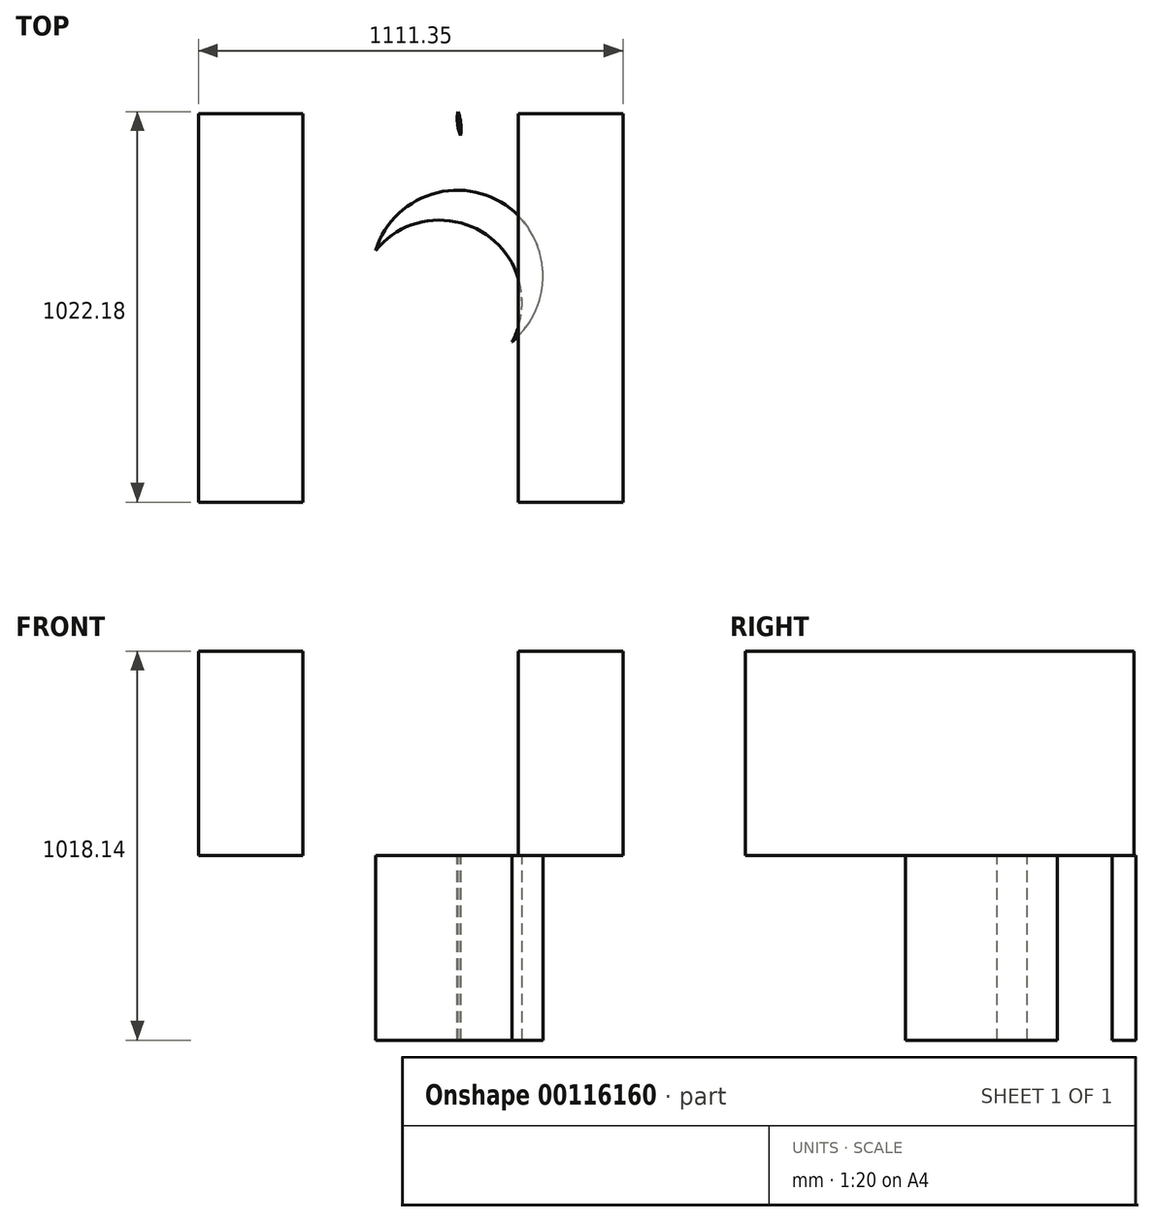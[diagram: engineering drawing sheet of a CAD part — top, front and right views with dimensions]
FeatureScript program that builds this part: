
annotation { "Feature Type Name" : "Feature", "Feature Type Description" : "" }
export const myFeature = defineFeature(function(context is Context, id is Id, definition is map)
    precondition{}
    {
        {
            var Q0;
            Q0=qCreatedBy(makeId("Front.planeOp"),FACE);
            var sketch = newSketch(context, id + "F0", { "sketchPlane" : qUnion([Q0])});
            skLineSegment(sketch, "E0.bottom", {"start": v(0, 0) * mm, "end": v(837.47, 0) * mm});
            skLineSegment(sketch, "E0.top", {"start": v(0, 535.38) * mm, "end": v(837.47, 535.38) * mm});
            skLineSegment(sketch, "E0.left", {"start": v(0, 0) * mm, "end": v(0, 535.38) * mm});
            skLineSegment(sketch, "E0.right", {"start": v(837.47, 0) * mm, "end": v(837.47, 535.38) * mm});
            skSolve(sketch);
        }
        {
            var Q0;
            Q0 = qSketchRegion(id + "F0", true);
            var Q1;
            Q1=sQuery(id+"F0.wireOp",EDGE,"E0.left");
            var Q2;
            Q2=sQuery(id+"F0.wireOp",EDGE,"E0.right");
            extrude(context, id + "F1", {"entities" : qUnion([Q0]), "bodyType" : ToolBodyType.SURFACE, "surfaceEntities" : qUnion([Q1, Q2]), "depth" : 1017.07 * mm});
        }
        {
            var Q0;
            Q0=qCreatedBy(makeId("Top.planeOp"),FACE);
            var sketch = newSketch(context, id + "F2", { "sketchPlane" : qUnion([Q0])});
            skArc(sketch, "E1", {"start": v(842.79, 0) * mm, "mid": v(81.24, 5.11) * mm, "end": v(547.08, -597.36) * mm});
            skArc(sketch, "E2", {"start": v(547.08, -597.36) * mm, "mid": v(489.15, -217.28) * mm, "end": v(180.8, -446.93) * mm});
            skArc(sketch, "E3", {"start": v(547.08, -597.36) * mm, "mid": v(477.47, -315.2) * mm, "end": v(189.96, -357.63) * mm});
            skArc(sketch, "E4", {"start": v(189.96, -75.06) * mm, "mid": v(81.98, -216.34) * mm, "end": v(189.96, -357.63) * mm});
            skArc(sketch, "E5", {"start": v(189.96, -75.06) * mm, "mid": v(403.04, -85.58) * mm, "end": v(256.29, 69.25) * mm});
            skArc(sketch, "E6", {"start": v(405.3, 5.11) * mm, "mid": v(558.05, -126.53) * mm, "end": v(606.3, 69.25) * mm});
            skSolve(sketch);
        }
        {
            var Q0;
            {var subQ0=sQuery(id+"F2.wireOp",EDGE,"E6");var subQ1=sQuery(id+"F2.wireOp",EDGE,"E5");var subQ2=makeQuery(id+"F2.imprint","INTERSECT",VERTEX,{"disambiguationData":[OD(0.0)],"derivedFrom":[subQ1,subQ0]});Q0=makeQuery(id+"F2.imprint","IMPRINT",FACE,{"disambiguationData":[TD([[makeQuery(id+"F2.imprint","IMPRINT",EDGE,{"disambiguationData":[TD([[subQ2,1.0]])],"derivedFrom":subQ1}),1.0]])]});}
            var Q1;
            {var subQ0=sQuery(id+"F2.wireOp",EDGE,"E3");Q1=makeQuery(id+"F2.imprint","IMPRINT",FACE,{"disambiguationData":[TD([[makeQuery(id+"F2.imprint","IMPRINT",EDGE,{"derivedFrom":subQ0}),-1.0]])]});}
            extrude(context, id + "F3", {"entities" : qUnion([Q0, Q1]), "oppositeDirection" : true, "depth" : 482.76 * mm});
        }
        {
            var Q0;
            Q0=makeQuery(id+"F1.opExtrude","SWEPT_FACE",FACE,{"disambiguationData":[OSD([sQuery(id+"F0.wireOp",EDGE,"E0.right")])]});
            var Q1;
            Q1=makeQuery(id+"F1.opExtrude","SWEPT_FACE",FACE,{"disambiguationData":[OSD([sQuery(id+"F0.wireOp",EDGE,"E0.left")])]});
            extrude(context, id + "F4", {"entities" : qUnion([Q0, Q1]), "operationType" : NewBodyOperationType.ADD, "oppositeDirection" : true, "depth" : 273.88 * mm});
        }
    });
